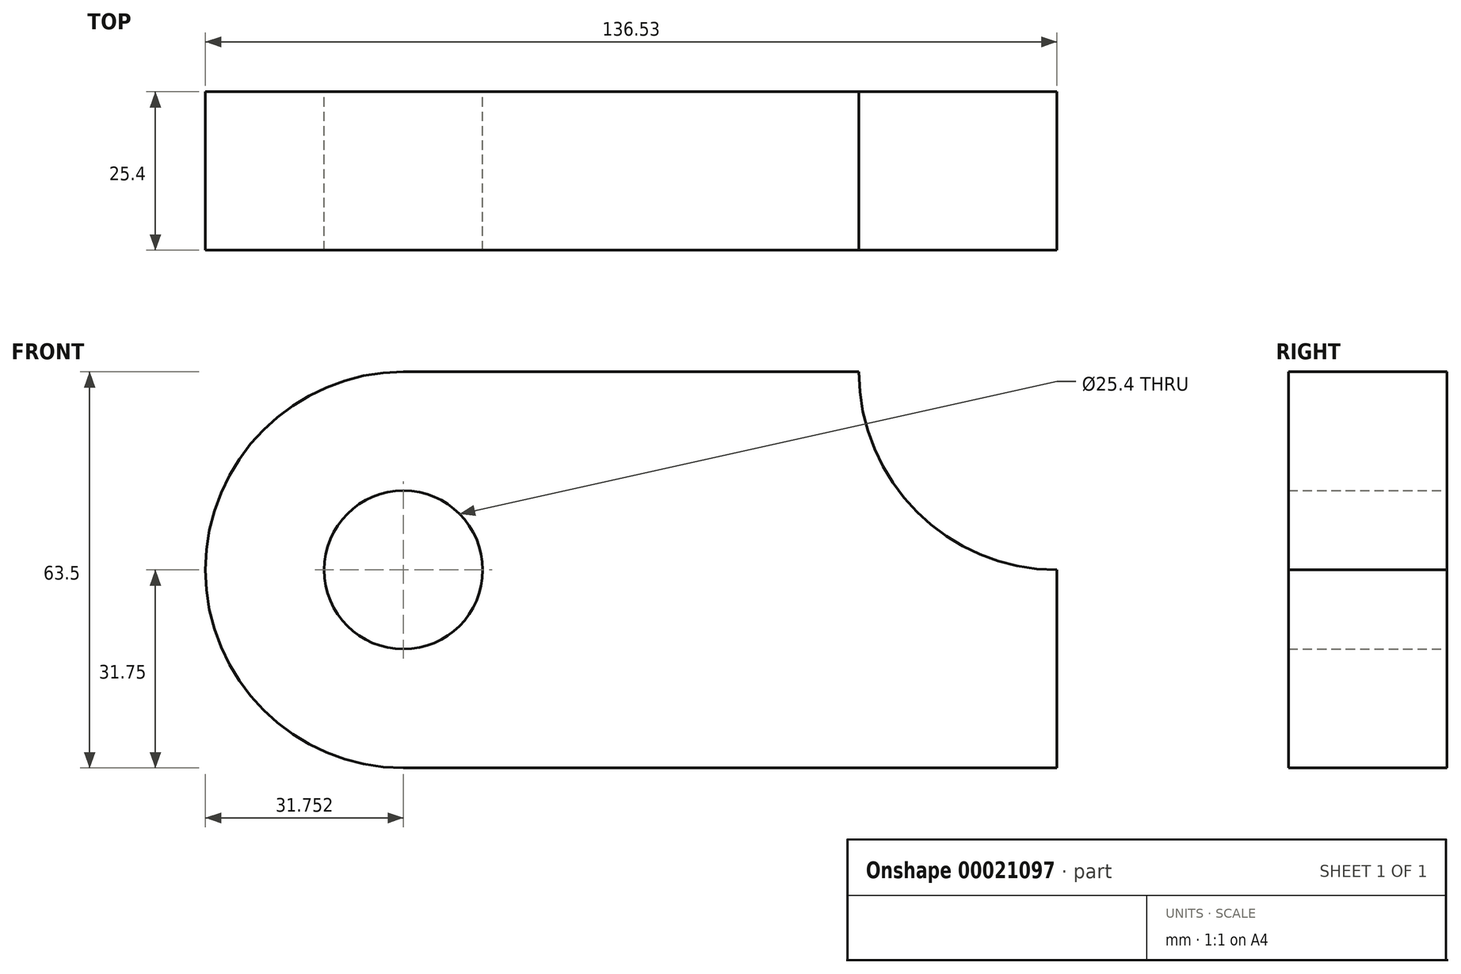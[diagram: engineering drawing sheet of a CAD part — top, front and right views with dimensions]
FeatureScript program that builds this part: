
annotation { "Feature Type Name" : "Feature", "Feature Type Description" : "" }
export const myFeature = defineFeature(function(context is Context, id is Id, definition is map)
    precondition{}
    {
        {
            var Q0;
            Q0=qCreatedBy(makeId("Front.planeOp"),FACE);
            var sketch = newSketch(context, id + "F0", { "sketchPlane" : qUnion([Q0])});
            skLineSegment(sketch, "E0.rect.bottom", {"start": v(-52.39, 31.75) * mm, "end": v(20.64, 31.75) * mm});
            skLineSegment(sketch, "E0.rect.top", {"start": v(-52.39, -31.75) * mm, "end": v(52.39, -31.75) * mm});
            skLineSegment(sketch, "E0.rect.left", {"start": v(-52.39, 31.75) * mm, "end": v(-52.39, -31.75) * mm});
            skLineSegment(sketch, "E0.rect.right", {"start": v(52.39, 0) * mm, "end": v(52.39, -31.75) * mm});
            skPoint(sketch, "E0.rect.middle", {"position": v(0, 0) * mm});
            skCircle(sketch, "E1", {"center": v(-52.39, 0) * mm, "radius": 31.75 * mm});
            skCircle(sketch, "E2", {"center": v(-52.39, 0) * mm, "radius": 12.7 * mm});
            skArc(sketch, "E3", {"start": v(20.64, 31.75) * mm, "mid": v(29.94, 9.3) * mm, "end": v(52.39, 0) * mm});
            skSolve(sketch);
        }
        {
            var Q0;
            {var subQ0=sQuery(id+"F0.wireOp",EDGE,"E2");var subQ1=sQuery(id+"F0.wireOp",EDGE,"E0.rect.left");var subQ3=makeQuery(id+"F0.imprint","INTERSECT",VERTEX,{"disambiguationData":[OD(0.0)],"derivedFrom":[subQ1,subQ0]});Q0=makeQuery(id+"F0.imprint","IMPRINT",FACE,{"disambiguationData":[TD([[makeQuery(id+"F0.imprint","IMPRINT",EDGE,{"disambiguationData":[TD([[subQ3,1.0]])],"derivedFrom":subQ0}),-1.0]])]});}
            var Q1;
            {var subQ0=sQuery(id+"F0.wireOp",EDGE,"E2");var subQ1=sQuery(id+"F0.wireOp",EDGE,"E0.rect.left");var subQ3=makeQuery(id+"F0.imprint","INTERSECT",VERTEX,{"disambiguationData":[OD(0.0)],"derivedFrom":[subQ1,subQ0]});Q1=makeQuery(id+"F0.imprint","IMPRINT",FACE,{"disambiguationData":[TD([[makeQuery(id+"F0.imprint","IMPRINT",EDGE,{"disambiguationData":[TD([[subQ3,-1.0]])],"derivedFrom":subQ0}),-1.0]])]});}
            var Q2;
            {var subQ3=sQuery(id+"F0.wireOp",EDGE,"E0.rect.bottom");Q2=makeQuery(id+"F0.imprint","IMPRINT",FACE,{"disambiguationData":[TD([[makeQuery(id+"F0.imprint","IMPRINT",EDGE,{"derivedFrom":subQ3}),-1.0]])]});}
            extrude(context, id + "F1", {"entities" : qUnion([Q0, Q1, Q2]), "depth" : 25.4 * mm});
        }
    });
